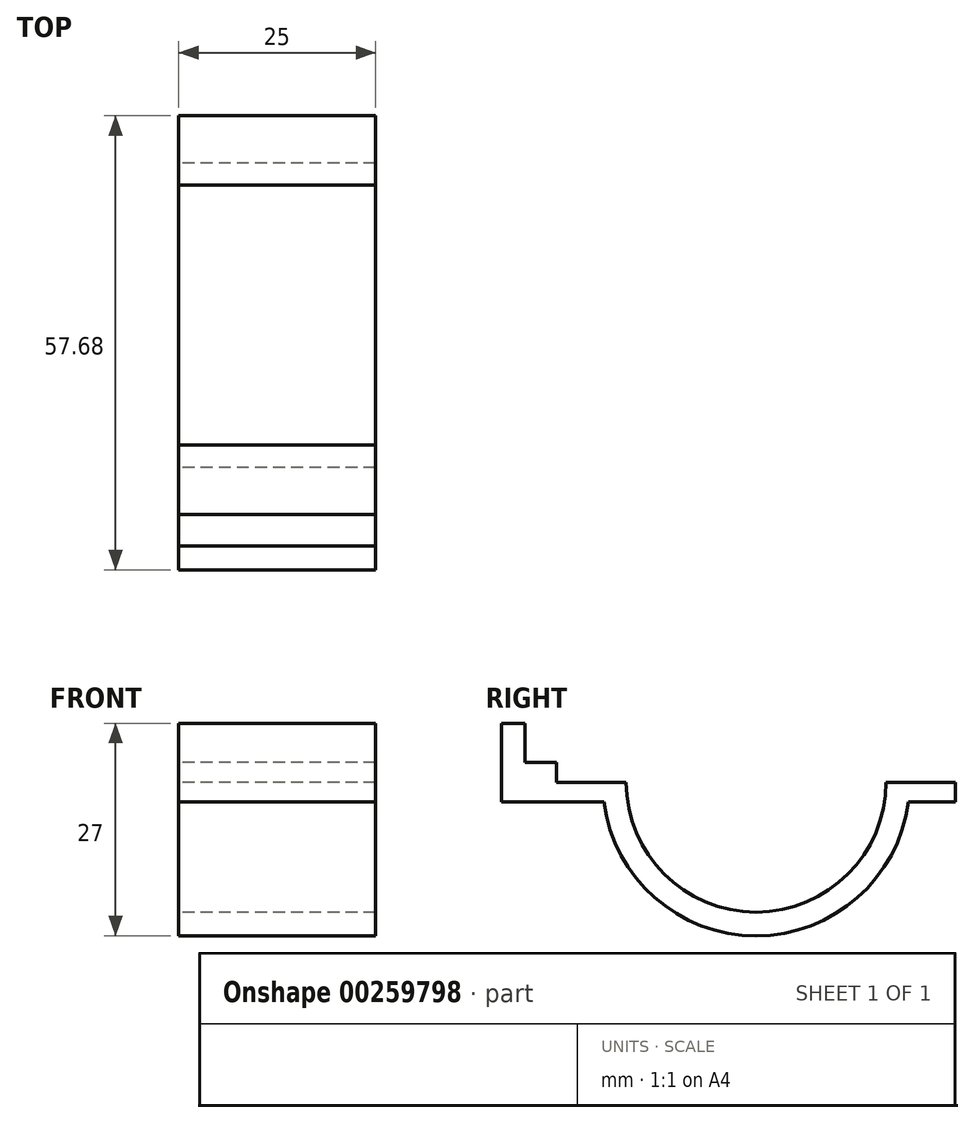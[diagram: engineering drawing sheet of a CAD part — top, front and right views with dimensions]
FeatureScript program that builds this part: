
annotation { "Feature Type Name" : "Feature", "Feature Type Description" : "" }
export const myFeature = defineFeature(function(context is Context, id is Id, definition is map)
    precondition{}
    {
        {
            var Q0;
            Q0=qCreatedBy(makeId("Right.planeOp"),FACE);
            var sketch = newSketch(context, id + "F0", { "sketchPlane" : qUnion([Q0])});
            skLineSegment(sketch, "E0", {"start": v(-32.34, 7.5) * mm, "end": v(-29.34, 7.5) * mm});
            skLineSegment(sketch, "E1", {"start": v(-29.34, 7.5) * mm, "end": v(-29.34, 2.5) * mm});
            skLineSegment(sketch, "E2", {"start": v(-32.34, 7.5) * mm, "end": v(-32.34, -2.5) * mm});
            skLineSegment(sketch, "E3", {"start": v(-29.34, 2.5) * mm, "end": v(-25.34, 2.5) * mm});
            skArc(sketch, "E4", {"start": v(-16.5, 0) * mm, "mid": v(0, -16.5) * mm, "end": v(16.5, 0) * mm});
            skArc(sketch, "E5", {"start": v(-19.34, -2.5) * mm, "mid": v(0, -19.5) * mm, "end": v(19.34, -2.5) * mm});
            skPoint(sketch, "E6.trimOffspring.end.orphan", {"position": v(11.87, 2.5) * mm});
            skLineSegment(sketch, "E7.trimOffspring", {"start": v(-19.34, -2.5) * mm, "end": v(-32.34, -2.5) * mm});
            skPoint(sketch, "E8.start.orphan", {"position": v(11.87, -2.5) * mm});
            skLineSegment(sketch, "E9", {"start": v(19.34, -2.5) * mm, "end": v(25.34, -2.5) * mm});
            skLineSegment(sketch, "E10", {"start": v(25.34, 0) * mm, "end": v(25.34, -2.5) * mm});
            skLineSegment(sketch, "E11", {"start": v(16.5, 0) * mm, "end": v(25.34, 0) * mm});
            skPoint(sketch, "E12.orphan", {"position": v(16.3, 2.5) * mm});
            skPoint(sketch, "E13.orphan", {"position": v(16.3, -2.5) * mm});
            skLineSegment(sketch, "E14", {"start": v(-16.5, 0) * mm, "end": v(-25.34, 0) * mm});
            skLineSegment(sketch, "E15", {"start": v(-25.34, 0) * mm, "end": v(-25.34, 2.5) * mm});
            skPoint(sketch, "E16.orphan", {"position": v(25.34, 2.5) * mm});
            skPoint(sketch, "E17.orphan", {"position": v(-19.34, 2.5) * mm});
            skSolve(sketch);
        }
        {
            var Q0;
            Q0=makeQuery(id+"F0.imprint","IMPRINT",FACE,{"disambiguationData":[TD([[makeQuery(id+"F0.imprint","IMPRINT",EDGE,{"derivedFrom":sQuery(id+"F0.wireOp",EDGE,"E0")}),-1.0]])]});
            extrude(context, id + "F1", {"entities" : qUnion([Q0]), "depth" : 25 * mm, "offsetDistance" : 25 * mm});
        }
    });
